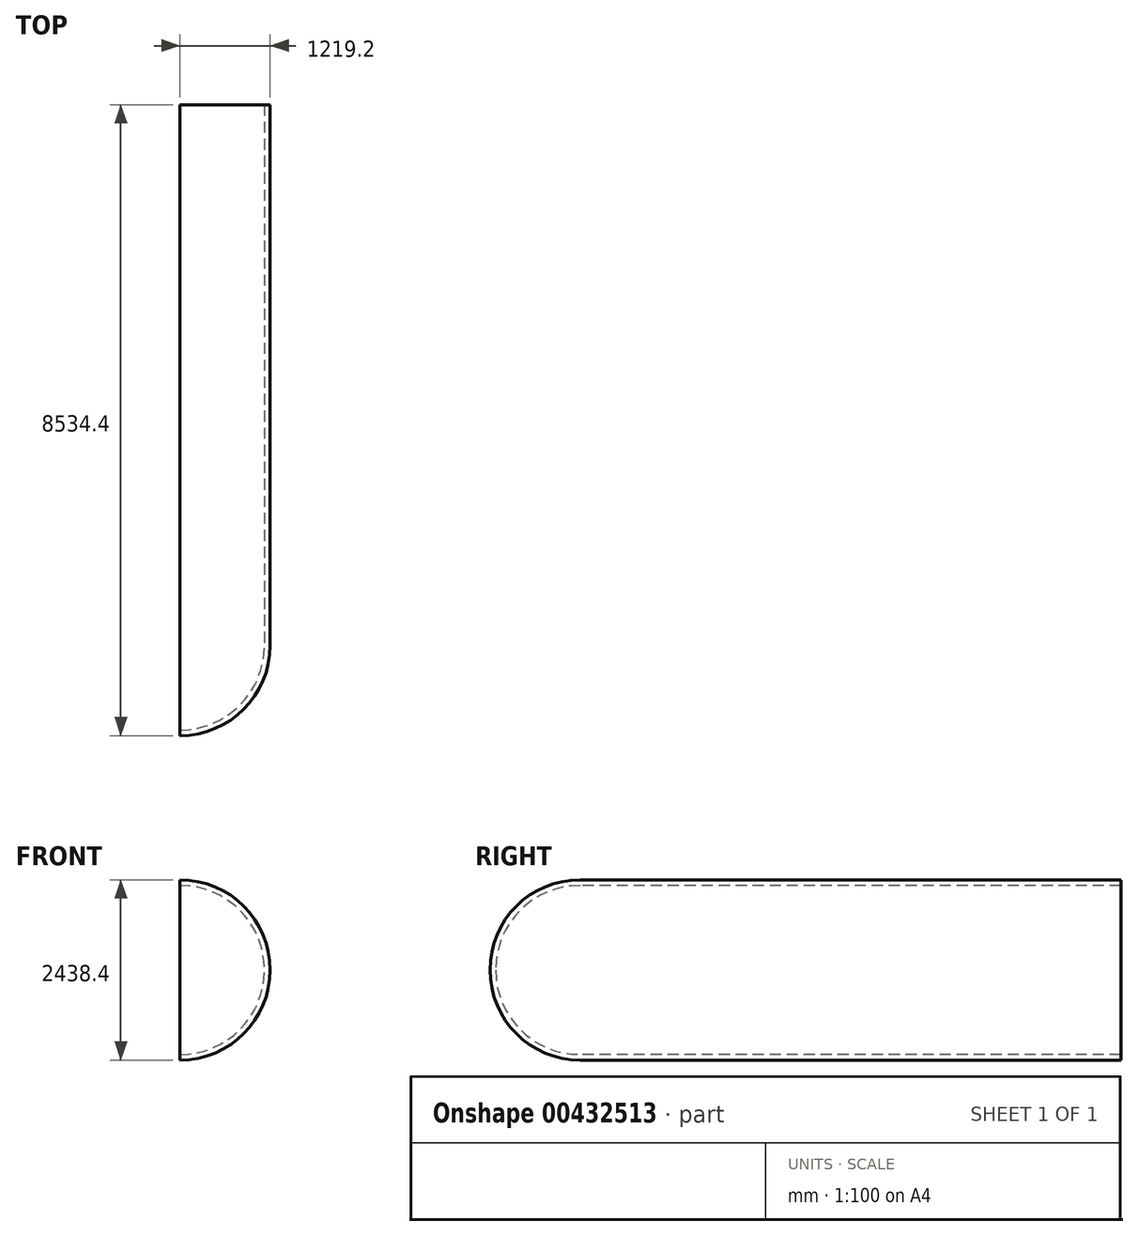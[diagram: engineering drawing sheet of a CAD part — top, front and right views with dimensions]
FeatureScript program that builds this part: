
annotation { "Feature Type Name" : "Feature", "Feature Type Description" : "" }
export const myFeature = defineFeature(function(context is Context, id is Id, definition is map)
    precondition{}
    {
        {
            var Q0;
            Q0=qCreatedBy(makeId("Right.planeOp"),FACE);
            var sketch = newSketch(context, id + "F0", { "sketchPlane" : qUnion([Q0])});
            skLineSegment(sketch, "E0.bottom", {"start": v(-3657.6, -1219.2) * mm, "end": v(3657.6, -1219.2) * mm});
            skLineSegment(sketch, "E0.top", {"start": v(-3657.6, 1219.2) * mm, "end": v(3657.6, 1219.2) * mm});
            skLineSegment(sketch, "E0.left", {"start": v(-3657.6, -1219.2) * mm, "end": v(-3657.6, 1219.2) * mm});
            skLineSegment(sketch, "E0.right", {"start": v(3657.6, -1219.2) * mm, "end": v(3657.6, 1219.2) * mm});
            skPoint(sketch, "E0.middle", {"position": v(0, 0) * mm});
            skLineSegment(sketch, "E1", {"start": v(-3657.6, 0) * mm, "end": v(3657.6, 0) * mm});
            skLineSegment(sketch, "E2", {"start": v(0, 1219.2) * mm, "end": v(0, -1219.2) * mm});
            skLineSegment(sketch, "E3", {"start": v(-1828.8, 1219.2) * mm, "end": v(-1828.8, -1219.2) * mm});
            skLineSegment(sketch, "E4", {"start": v(-914.4, 1219.2) * mm, "end": v(-914.4, -1219.2) * mm});
            skArc(sketch, "E5", {"start": v(-3657.6, -1219.2) * mm, "mid": v(-4876.8, 0) * mm, "end": v(-3657.6, 1219.2) * mm});
            skLineSegment(sketch, "E6.MirrorCS", {"start": v(914.4, 1219.2) * mm, "end": v(914.4, -1219.2) * mm});
            skLineSegment(sketch, "E7.MirrorCS", {"start": v(1828.8, 1219.2) * mm, "end": v(1828.8, -1219.2) * mm});
            skLineSegment(sketch, "E8.MirrorCS", {"start": v(2743.2, 1219.2) * mm, "end": v(2743.2, -1219.2) * mm});
            skLineSegment(sketch, "E9.MirrorCS", {"start": v(-2743.2, 1219.2) * mm, "end": v(-2743.2, -1219.2) * mm});
            skLineSegment(sketch, "E10.MirrorCS", {"start": v(-3657.6, 1219.2) * mm, "end": v(-3657.6, -1219.2) * mm});
            skLineSegment(sketch, "E11.MirrorCS", {"start": v(-4572, 1219.2) * mm, "end": v(-4572, -1219.2) * mm});
            skLineSegment(sketch, "E12", {"start": v(3657.6, 0) * mm, "end": v(4572, 0) * mm});
            skLineSegment(sketch, "E13", {"start": v(3657.6, 609.6) * mm, "end": v(-4713.46, 609.6) * mm});
            skLineSegment(sketch, "E14", {"start": v(3657.6, 914.4) * mm, "end": v(2743.2, 914.4) * mm});
            skPoint(sketch, "E14.startSnap0", {"position": v(3200.4, 914.4) * mm});
            skLineSegment(sketch, "E15", {"start": v(3657.6, 1066.8) * mm, "end": v(2743.2, 1066.8) * mm});
            skPoint(sketch, "E15.startSnap0", {"position": v(3200.4, 1066.8) * mm});
            skLineSegment(sketch, "E16", {"start": v(3657.6, 1143) * mm, "end": v(2743.2, 1143) * mm});
            skPoint(sketch, "E16.startSnap0", {"position": v(3200.4, 1143) * mm});
            skLineSegment(sketch, "E17", {"start": v(2743.2, 1066.8) * mm, "end": v(-3657.6, 1066.8) * mm});
            skArc(sketch, "E18", {"start": v(-3657.6, 1066.8) * mm, "mid": v(-4724.4, 0) * mm, "end": v(-3657.6, -1066.8) * mm});
            skLineSegment(sketch, "E19", {"start": v(-3657.6, -1066.8) * mm, "end": v(3657.6, -1066.8) * mm});
            skLineSegment(sketch, "E20", {"start": v(4572, -1066.8) * mm, "end": v(4572, -914.4) * mm});
            skLineSegment(sketch, "E21", {"start": v(4572, -914.4) * mm, "end": v(3657.6, -1066.8) * mm});
            skLineSegment(sketch, "E22", {"start": v(4572, -1066.8) * mm, "end": v(3657.6, -1219.2) * mm});
            skLineSegment(sketch, "E23", {"start": v(4572, 0) * mm, "end": v(4572, -914.4) * mm});
            skLineSegment(sketch, "E24", {"start": v(3657.6, 1066.8) * mm, "end": v(4572, 1066.8) * mm});
            skLineSegment(sketch, "E25", {"start": v(4572, 1066.8) * mm, "end": v(3657.6, 1219.2) * mm});
            skCircle(sketch, "E26", {"center": v(0, 0) * mm, "radius": 1066.8 * mm});
            skLineSegment(sketch, "E27", {"start": v(-4876.8, 0) * mm, "end": v(-4876.8, -1561.92) * mm});
            skLineSegment(sketch, "E28", {"start": v(2743.2, 1143) * mm, "end": v(-3657.6, 1143) * mm});
            skLineSegment(sketch, "E29", {"start": v(3657.6, -1143) * mm, "end": v(-3657.6, -1143) * mm});
            skArc(sketch, "E30", {"start": v(-3657.6, -1143) * mm, "mid": v(-4800.6, 0) * mm, "end": v(-3657.6, 1143) * mm});
            skLineSegment(sketch, "E31.MirrorCS", {"start": v(-3657.6, -762) * mm, "end": v(3657.6, -762) * mm});
            skLineSegment(sketch, "E32", {"start": v(-746.6, -762) * mm, "end": v(-746.6, 762) * mm});
            skLineSegment(sketch, "E33", {"start": v(0, -762) * mm, "end": v(0, 1066.8) * mm});
            skLineSegment(sketch, "E34", {"start": v(-1797.7, -3927.66) * mm, "end": v(-1774.84, -3927.66) * mm});
            skLineSegment(sketch, "E35", {"start": v(-1797.7, -3927.66) * mm, "end": v(-1797.7, -3930.2) * mm});
            skLineSegment(sketch, "E36", {"start": v(-1797.7, -3930.2) * mm, "end": v(-1772.8, -3930.2) * mm});
            skLineSegment(sketch, "E37", {"start": v(-1769.76, -3914.96) * mm, "end": v(-1769.76, -3912.42) * mm});
            skLineSegment(sketch, "E38", {"start": v(-1846.8, -3914.96) * mm, "end": v(-1846.8, -3912.42) * mm});
            skLineSegment(sketch, "E39", {"start": v(-1774.84, -3914.96) * mm, "end": v(-1774.84, -3927.66) * mm});
            skLineSegment(sketch, "E40", {"start": v(-1769.76, -3914.96) * mm, "end": v(-1772.8, -3930.2) * mm});
            skLineSegment(sketch, "E41", {"start": v(-1846.8, -3912.42) * mm, "end": v(-1769.76, -3912.42) * mm});
            skLineSegment(sketch, "E42", {"start": v(-1846.8, -3914.96) * mm, "end": v(-1774.84, -3914.96) * mm});
            skLineSegment(sketch, "E43.MirrorCS", {"start": v(-1769.76, -3914.96) * mm, "end": v(-1766.7, -3930.2) * mm});
            skLineSegment(sketch, "E44.MirrorCS", {"start": v(-1741.82, -3930.2) * mm, "end": v(-1766.7, -3930.2) * mm});
            skLineSegment(sketch, "E45.MirrorCS", {"start": v(-1741.82, -3927.66) * mm, "end": v(-1741.82, -3930.2) * mm});
            skLineSegment(sketch, "E46.MirrorCS", {"start": v(-1741.82, -3927.66) * mm, "end": v(-1764.68, -3927.66) * mm});
            skLineSegment(sketch, "E47.MirrorCS", {"start": v(-1764.68, -3914.96) * mm, "end": v(-1764.68, -3927.66) * mm});
            skLineSegment(sketch, "E48", {"start": v(-1772.55, -3930.2) * mm, "end": v(-1770.52, -3920.04) * mm});
            skLineSegment(sketch, "E49", {"start": v(-1772.55, -3930.2) * mm, "end": v(-1772.6, -3930.45) * mm});
            skLineSegment(sketch, "E50", {"start": v(-1772.6, -3930.45) * mm, "end": v(-1798, -3930.45) * mm});
            skLineSegment(sketch, "E51", {"start": v(-1798, -3930.45) * mm, "end": v(-1798, -3927.4) * mm});
            skLineSegment(sketch, "E52", {"start": v(-1798, -3927.4) * mm, "end": v(-1775.14, -3927.4) * mm});
            skLineSegment(sketch, "E53", {"start": v(-1775.14, -3927.4) * mm, "end": v(-1775.14, -3915.2) * mm});
            skLineSegment(sketch, "E54", {"start": v(-1775.14, -3915.2) * mm, "end": v(-1813.24, -3915.2) * mm});
            skLineSegment(sketch, "E55.MirrorCS", {"start": v(-1766.96, -3930.2) * mm, "end": v(-1769, -3920.04) * mm});
            skLineSegment(sketch, "E56.MirrorCS", {"start": v(-1766.91, -3930.45) * mm, "end": v(-1741.51, -3930.45) * mm});
            skLineSegment(sketch, "E57.MirrorCS", {"start": v(-1741.51, -3930.45) * mm, "end": v(-1741.51, -3927.4) * mm});
            skLineSegment(sketch, "E58.MirrorCS", {"start": v(-1741.51, -3927.4) * mm, "end": v(-1764.37, -3927.4) * mm});
            skLineSegment(sketch, "E59.MirrorCS", {"start": v(-1764.37, -3927.4) * mm, "end": v(-1764.37, -3915.2) * mm});
            skLineSegment(sketch, "E60.MirrorCS", {"start": v(-1764.37, -3915.2) * mm, "end": v(-1726.27, -3915.2) * mm});
            skLineSegment(sketch, "E61", {"start": v(-1769, -3920.04) * mm, "end": v(-1770.52, -3920.04) * mm});
            skLineSegment(sketch, "E62", {"start": v(-1766.91, -3930.45) * mm, "end": v(-1766.96, -3930.2) * mm});
            skLineSegment(sketch, "E63", {"start": v(-1813.24, -3935.52) * mm, "end": v(-1726.27, -3935.52) * mm});
            skLineSegment(sketch, "E64", {"start": v(-1813.24, -3935.52) * mm, "end": v(-1813.24, -3915.2) * mm});
            skLineSegment(sketch, "E65", {"start": v(-1726.27, -3915.2) * mm, "end": v(-1726.27, -3935.52) * mm});
            skCircle(sketch, "E66", {"center": v(-8660.7, 0) * mm, "radius": 1219.2 * mm});
            skLineSegment(sketch, "E67", {"start": v(-8660.7, 0) * mm, "end": v(-8660.7, 1219.2) * mm});
            skLineSegment(sketch, "E68", {"start": v(-8660.7, 0) * mm, "end": v(-8660.7, -1219.2) * mm});
            skLineSegment(sketch, "E69", {"start": v(-7441.5, 0) * mm, "end": v(-8660.7, 0) * mm});
            skLineSegment(sketch, "E70", {"start": v(-8051.1, -609.6) * mm, "end": v(-8660.7, -609.6) * mm});
            skPoint(sketch, "E70.startSnap0", {"position": v(-8051.1, 0) * mm});
            skPoint(sketch, "E70.startSnap1", {"position": v(-8660.7, -609.6) * mm});
            skLineSegment(sketch, "E71", {"start": v(-8355.9, -1180.49) * mm, "end": v(-8355.9, -609.6) * mm});
            skPoint(sketch, "E71.startSnap0", {"position": v(-8355.9, -609.6) * mm});
            skLineSegment(sketch, "E72", {"start": v(-8355.9, -895.04) * mm, "end": v(-7832.84, -895.04) * mm});
            skLineSegment(sketch, "E73", {"start": v(-8094.37, -1079.69) * mm, "end": v(-8094.37, -895.04) * mm});
            skPoint(sketch, "E73.startSnap0", {"position": v(-8094.37, -895.04) * mm});
            skLineSegment(sketch, "E74", {"start": v(-8355.9, -609.6) * mm, "end": v(-8355.9, 0) * mm});
            skLineSegment(sketch, "E75", {"start": v(-8355.9, 0) * mm, "end": v(-8051.1, 0) * mm});
            skLineSegment(sketch, "E76", {"start": v(-8051.1, -609.6) * mm, "end": v(-8051.1, 0) * mm});
            skLineSegment(sketch, "E77", {"start": v(-8051.1, -1055.86) * mm, "end": v(-8051.1, -609.6) * mm});
            skLineSegment(sketch, "E78", {"start": v(-8051.1, -609.6) * mm, "end": v(-7441.5, 0) * mm});
            skLineSegment(sketch, "E79", {"start": v(-7746.3, -304.8) * mm, "end": v(-7746.3, 0) * mm});
            skLineSegment(sketch, "E80", {"start": v(-7746.3, 0) * mm, "end": v(-7746.3, -806.42) * mm});
            skLineSegment(sketch, "E81", {"start": v(-8660.7, -304.8) * mm, "end": v(-7480.21, -304.8) * mm});
            skPoint(sketch, "E81.startSnap0", {"position": v(-8355.9, -304.8) * mm});
            skLineSegment(sketch, "E82", {"start": v(-8051.1, -609.6) * mm, "end": v(-7604.84, -609.6) * mm});
            skLineSegment(sketch, "E83.bottom", {"start": v(7784.68, -1157.92) * mm, "end": v(15099.88, -1157.92) * mm});
            skLineSegment(sketch, "E83.top", {"start": v(7784.68, 1280.48) * mm, "end": v(15099.88, 1280.48) * mm});
            skLineSegment(sketch, "E83.left", {"start": v(7784.68, -1157.92) * mm, "end": v(7784.68, 1280.48) * mm});
            skLineSegment(sketch, "E83.right", {"start": v(15099.88, -1157.92) * mm, "end": v(15099.88, 1280.48) * mm});
            skLineSegment(sketch, "E84", {"start": v(9613.48, 1280.48) * mm, "end": v(9613.48, -1157.92) * mm});
            skLineSegment(sketch, "E85", {"start": v(10527.88, 1280.48) * mm, "end": v(10527.88, -1157.92) * mm});
            skArc(sketch, "E86", {"start": v(7784.68, -1157.92) * mm, "mid": v(6565.48, 61.28) * mm, "end": v(7784.68, 1280.48) * mm});
            skLineSegment(sketch, "E87.MirrorCS", {"start": v(12356.68, 1280.48) * mm, "end": v(12356.68, -1157.92) * mm});
            skLineSegment(sketch, "E88.MirrorCS", {"start": v(13271.08, 1280.48) * mm, "end": v(13271.08, -1157.92) * mm});
            skLineSegment(sketch, "E89.MirrorCS", {"start": v(14185.48, 1280.48) * mm, "end": v(14185.48, -1157.92) * mm});
            skLineSegment(sketch, "E90.MirrorCS", {"start": v(8699.08, 1280.48) * mm, "end": v(8699.08, -1157.92) * mm});
            skLineSegment(sketch, "E91.MirrorCS", {"start": v(7784.68, 1280.48) * mm, "end": v(7784.68, -1157.92) * mm});
            skLineSegment(sketch, "E92.MirrorCS", {"start": v(6870.28, 610.76) * mm, "end": v(6870.28, -488.2) * mm});
            skLineSegment(sketch, "E93", {"start": v(15099.88, 61.28) * mm, "end": v(16014.28, 61.28) * mm});
            skLineSegment(sketch, "E94", {"start": v(15099.88, 1128.08) * mm, "end": v(14185.48, 1128.08) * mm});
            skLineSegment(sketch, "E95", {"start": v(15099.88, 1204.28) * mm, "end": v(14185.48, 1204.28) * mm});
            skLineSegment(sketch, "E96", {"start": v(14185.48, 1128.08) * mm, "end": v(7784.68, 1128.08) * mm});
            skArc(sketch, "E97", {"start": v(7784.68, 1128.08) * mm, "mid": v(6717.88, 61.28) * mm, "end": v(7784.68, -1005.52) * mm});
            skLineSegment(sketch, "E98", {"start": v(7784.68, -1005.52) * mm, "end": v(15099.88, -1005.52) * mm});
            skLineSegment(sketch, "E99", {"start": v(16014.28, -1005.52) * mm, "end": v(16014.28, -853.12) * mm});
            skLineSegment(sketch, "E100", {"start": v(16014.28, -853.12) * mm, "end": v(15099.88, -1005.52) * mm});
            skLineSegment(sketch, "E101", {"start": v(16014.28, -1005.52) * mm, "end": v(15099.88, -1157.92) * mm});
            skLineSegment(sketch, "E102", {"start": v(16014.28, 61.28) * mm, "end": v(16014.28, -853.12) * mm});
            skLineSegment(sketch, "E103", {"start": v(15099.88, 1128.08) * mm, "end": v(16014.28, 1128.08) * mm});
            skLineSegment(sketch, "E104", {"start": v(16014.28, 1128.08) * mm, "end": v(15099.88, 1280.48) * mm});
            skLineSegment(sketch, "E105", {"start": v(14185.48, 1204.28) * mm, "end": v(7784.68, 1204.28) * mm});
            skLineSegment(sketch, "E106", {"start": v(15099.88, -1081.72) * mm, "end": v(7784.68, -1081.72) * mm});
            skArc(sketch, "E107", {"start": v(7784.68, -1081.72) * mm, "mid": v(6641.68, 61.28) * mm, "end": v(7784.68, 1204.28) * mm});
            skLineSegment(sketch, "E108", {"start": v(11442.28, -1157.92) * mm, "end": v(11442.28, 1280.48) * mm});
            skLineSegment(sketch, "E109", {"start": v(-1726.27, -3935.52) * mm, "end": v(-1726.27, -3948.21) * mm});
            skLineSegment(sketch, "E110.MirrorCS", {"start": v(-1639.3, -3935.52) * mm, "end": v(-1726.27, -3935.52) * mm});
            skLineSegment(sketch, "E111.MirrorCS", {"start": v(-1711.03, -3930.45) * mm, "end": v(-1711.03, -3927.4) * mm});
            skLineSegment(sketch, "E112.MirrorCS", {"start": v(-1685.63, -3930.45) * mm, "end": v(-1711.03, -3930.45) * mm});
            skLineSegment(sketch, "E113.MirrorCS", {"start": v(-1710.73, -3930.2) * mm, "end": v(-1685.84, -3930.2) * mm});
            skLineSegment(sketch, "E114.MirrorCS", {"start": v(-1710.73, -3927.66) * mm, "end": v(-1710.73, -3930.2) * mm});
            skLineSegment(sketch, "E115.MirrorCS", {"start": v(-1710.73, -3927.66) * mm, "end": v(-1687.87, -3927.66) * mm});
            skLineSegment(sketch, "E116.MirrorCS", {"start": v(-1711.03, -3927.4) * mm, "end": v(-1688.17, -3927.4) * mm});
            skLineSegment(sketch, "E117.MirrorCS", {"start": v(-1688.17, -3927.4) * mm, "end": v(-1688.17, -3915.2) * mm});
            skLineSegment(sketch, "E118.MirrorCS", {"start": v(-1687.87, -3914.96) * mm, "end": v(-1687.87, -3927.66) * mm});
            skLineSegment(sketch, "E119.MirrorCS", {"start": v(-1682.79, -3914.96) * mm, "end": v(-1685.84, -3930.2) * mm});
            skLineSegment(sketch, "E120.MirrorCS", {"start": v(-1682.79, -3914.96) * mm, "end": v(-1682.79, -3912.42) * mm});
            skLineSegment(sketch, "E121.MirrorCS", {"start": v(-1688.17, -3915.2) * mm, "end": v(-1726.27, -3915.2) * mm});
            skLineSegment(sketch, "E122.MirrorCS", {"start": v(-1683.55, -3920.04) * mm, "end": v(-1682.03, -3920.04) * mm});
            skLineSegment(sketch, "E123.MirrorCS", {"start": v(-1685.58, -3930.2) * mm, "end": v(-1683.55, -3920.04) * mm});
            skLineSegment(sketch, "E124.MirrorCS", {"start": v(-1680, -3930.2) * mm, "end": v(-1682.03, -3920.04) * mm});
            skLineSegment(sketch, "E125.MirrorCS", {"start": v(-1679.94, -3930.45) * mm, "end": v(-1654.54, -3930.45) * mm});
            skLineSegment(sketch, "E126.MirrorCS", {"start": v(-1654.85, -3930.2) * mm, "end": v(-1679.74, -3930.2) * mm});
            skLineSegment(sketch, "E127.MirrorCS", {"start": v(-1654.54, -3927.4) * mm, "end": v(-1677.4, -3927.4) * mm});
            skLineSegment(sketch, "E128.MirrorCS", {"start": v(-1654.85, -3927.66) * mm, "end": v(-1677.7, -3927.66) * mm});
            skLineSegment(sketch, "E129.MirrorCS", {"start": v(-1677.4, -3927.4) * mm, "end": v(-1677.4, -3915.2) * mm});
            skLineSegment(sketch, "E130.MirrorCS", {"start": v(-1677.7, -3914.96) * mm, "end": v(-1677.7, -3927.66) * mm});
            skLineSegment(sketch, "E131.MirrorCS", {"start": v(-1677.4, -3915.2) * mm, "end": v(-1639.3, -3915.2) * mm});
            skLineSegment(sketch, "E132.MirrorCS", {"start": v(-1605.74, -3914.96) * mm, "end": v(-1677.7, -3914.96) * mm});
            skLineSegment(sketch, "E133.MirrorCS", {"start": v(-1605.74, -3912.42) * mm, "end": v(-1682.79, -3912.42) * mm});
            skLineSegment(sketch, "E134.MirrorCS", {"start": v(-1682.79, -3914.96) * mm, "end": v(-1679.74, -3930.2) * mm});
            skLineSegment(sketch, "E135.MirrorCS", {"start": v(-1639.3, -3935.52) * mm, "end": v(-1639.3, -3915.2) * mm});
            skLineSegment(sketch, "E136.MirrorCS", {"start": v(-1605.74, -3914.96) * mm, "end": v(-1605.74, -3912.42) * mm});
            skLineSegment(sketch, "E137", {"start": v(-1769.76, -3912.42) * mm, "end": v(-1682.79, -3912.42) * mm});
            skLineSegment(sketch, "E138", {"start": v(-1764.68, -3914.96) * mm, "end": v(-1687.87, -3914.96) * mm});
            skLineSegment(sketch, "E139", {"start": v(-1654.85, -3927.66) * mm, "end": v(-1654.85, -3930.2) * mm});
            skLineSegment(sketch, "E140", {"start": v(-1654.54, -3927.4) * mm, "end": v(-1654.54, -3930.45) * mm});
            skLineSegment(sketch, "E141", {"start": v(-1685.63, -3930.45) * mm, "end": v(-1685.58, -3930.2) * mm});
            skLineSegment(sketch, "E142", {"start": v(-1679.94, -3930.45) * mm, "end": v(-1680, -3930.2) * mm});
            skLineSegment(sketch, "E143", {"start": v(-1592.05, -3912.42) * mm, "end": v(-1592.05, -3937.82) * mm, "construction": true});
            skLineSegment(sketch, "E144", {"start": v(-1592.05, -3937.82) * mm, "end": v(-1592.05, -3963.22) * mm, "construction": true});
            skLineSegment(sketch, "E145", {"start": v(-1592.05, -3963.22) * mm, "end": v(-1592.05, -3988.62) * mm, "construction": true});
            skLineSegment(sketch, "E146", {"start": v(-1639.3, -3921.3) * mm, "end": v(-1635.47, -3921.3) * mm});
            skPoint(sketch, "E146.startSnap0", {"position": v(-1677.4, -3921.3) * mm});
            skPoint(sketch, "E146.endSnap0", {"position": v(-1677.4, -3921.3) * mm});
            skLineSegment(sketch, "E147", {"start": v(-1635.47, -3921.3) * mm, "end": v(-1635.47, -3922.57) * mm});
            skLineSegment(sketch, "E148.MirrorCS", {"start": v(-1635.47, -3921.3) * mm, "end": v(-1635.47, -3920.03) * mm});
            skLineSegment(sketch, "E149", {"start": v(-1635.47, -3920.03) * mm, "end": v(-1677.4, -3920.03) * mm});
            skLineSegment(sketch, "E150", {"start": v(-1677.4, -3920.03) * mm, "end": v(-1677.4, -3922.57) * mm});
            skLineSegment(sketch, "E151", {"start": v(-1677.4, -3922.57) * mm, "end": v(-1635.47, -3922.57) * mm});
            skLineSegment(sketch, "E152", {"start": v(-1685.58, -3930.2) * mm, "end": v(-1686.65, -3935.52) * mm});
            skLineSegment(sketch, "E153", {"start": v(-1686.65, -3935.52) * mm, "end": v(-1683.55, -3930.2) * mm});
            skLineSegment(sketch, "E154", {"start": v(-1683.55, -3930.2) * mm, "end": v(-1682.03, -3930.2) * mm});
            skLineSegment(sketch, "E155.MirrorCS", {"start": v(-1678.93, -3935.52) * mm, "end": v(-1682.03, -3930.2) * mm});
            skLineSegment(sketch, "E156.MirrorCS", {"start": v(-1680, -3930.2) * mm, "end": v(-1678.93, -3935.52) * mm});
            skLineSegment(sketch, "E157", {"start": v(6717.88, 61.28) * mm, "end": v(6565.48, 61.28) * mm});
            skSolve(sketch);
        }
        {
            var Q0;
            {var subQ1=sQuery(id+"F0.wireOp",EDGE,"E86");var subQ3=sQuery(id+"F0.wireOp",EDGE,"E157");var subQ4=makeQuery(id+"F0.imprint","INTERSECT",VERTEX,{"derivedFrom":[subQ1,subQ3]});Q0=makeQuery(id+"F0.imprint","IMPRINT",FACE,{"disambiguationData":[TD([[makeQuery(id+"F0.imprint","IMPRINT",EDGE,{"disambiguationData":[TD([[subQ4,1.0]])],"derivedFrom":subQ3}),-1.0]])]});}
            var Q1;
            {var subQ1=sQuery(id+"F0.wireOp",EDGE,"E83.top");var subQ3=sQuery(id+"F0.wireOp",EDGE,"E90.MirrorCS");var subQ4=makeQuery(id+"F0.imprint","INTERSECT",VERTEX,{"derivedFrom":[subQ1,subQ3]});Q1=makeQuery(id+"F0.imprint","IMPRINT",FACE,{"disambiguationData":[TD([[makeQuery(id+"F0.imprint","IMPRINT",EDGE,{"disambiguationData":[TD([[subQ4,-1.0]])],"derivedFrom":subQ3}),-1.0]])]});}
            var Q2;
            {var subQ0=sQuery(id+"F0.wireOp",EDGE,"E84");var subQ1=sQuery(id+"F0.wireOp",EDGE,"E83.top");var subQ2=makeQuery(id+"F0.imprint","INTERSECT",VERTEX,{"derivedFrom":[subQ1,subQ0]});Q2=makeQuery(id+"F0.imprint","IMPRINT",FACE,{"disambiguationData":[TD([[makeQuery(id+"F0.imprint","IMPRINT",EDGE,{"disambiguationData":[TD([[subQ2,1.0]])],"derivedFrom":subQ1}),-1.0]])]});}
            var Q3;
            {var subQ0=sQuery(id+"F0.wireOp",EDGE,"E84");var subQ1=sQuery(id+"F0.wireOp",EDGE,"E83.top");var subQ2=makeQuery(id+"F0.imprint","INTERSECT",VERTEX,{"derivedFrom":[subQ1,subQ0]});Q3=makeQuery(id+"F0.imprint","IMPRINT",FACE,{"disambiguationData":[TD([[makeQuery(id+"F0.imprint","IMPRINT",EDGE,{"disambiguationData":[TD([[subQ2,-1.0]])],"derivedFrom":subQ1}),-1.0]])]});}
            var Q4;
            {var subQ0=sQuery(id+"F0.wireOp",EDGE,"E85");var subQ1=sQuery(id+"F0.wireOp",EDGE,"E83.top");var subQ2=makeQuery(id+"F0.imprint","INTERSECT",VERTEX,{"derivedFrom":[subQ1,subQ0]});Q4=makeQuery(id+"F0.imprint","IMPRINT",FACE,{"disambiguationData":[TD([[makeQuery(id+"F0.imprint","IMPRINT",EDGE,{"disambiguationData":[TD([[subQ2,-1.0]])],"derivedFrom":subQ1}),-1.0]])]});}
            var Q5;
            {var subQ0=sQuery(id+"F0.wireOp",EDGE,"E87.MirrorCS");var subQ1=sQuery(id+"F0.wireOp",EDGE,"E83.top");var subQ2=makeQuery(id+"F0.imprint","INTERSECT",VERTEX,{"derivedFrom":[subQ1,subQ0]});Q5=makeQuery(id+"F0.imprint","IMPRINT",FACE,{"disambiguationData":[TD([[makeQuery(id+"F0.imprint","IMPRINT",EDGE,{"disambiguationData":[TD([[subQ2,1.0]])],"derivedFrom":subQ1}),-1.0]])]});}
            var Q6;
            {var subQ0=sQuery(id+"F0.wireOp",EDGE,"E87.MirrorCS");var subQ1=sQuery(id+"F0.wireOp",EDGE,"E83.top");var subQ2=makeQuery(id+"F0.imprint","INTERSECT",VERTEX,{"derivedFrom":[subQ1,subQ0]});Q6=makeQuery(id+"F0.imprint","IMPRINT",FACE,{"disambiguationData":[TD([[makeQuery(id+"F0.imprint","IMPRINT",EDGE,{"disambiguationData":[TD([[subQ2,-1.0]])],"derivedFrom":subQ1}),-1.0]])]});}
            var Q7;
            {var subQ0=sQuery(id+"F0.wireOp",EDGE,"E88.MirrorCS");var subQ1=sQuery(id+"F0.wireOp",EDGE,"E83.top");var subQ2=makeQuery(id+"F0.imprint","INTERSECT",VERTEX,{"derivedFrom":[subQ1,subQ0]});Q7=makeQuery(id+"F0.imprint","IMPRINT",FACE,{"disambiguationData":[TD([[makeQuery(id+"F0.imprint","IMPRINT",EDGE,{"disambiguationData":[TD([[subQ2,-1.0]])],"derivedFrom":subQ1}),-1.0]])]});}
            var Q8;
            {var subQ5=sQuery(id+"F0.wireOp",EDGE,"E95");Q8=makeQuery(id+"F0.imprint","IMPRINT",FACE,{"disambiguationData":[TD([[makeQuery(id+"F0.imprint","IMPRINT",EDGE,{"derivedFrom":subQ5}),-1.0]])]});}
            var Q9;
            Q9=sQuery(id+"F0.wireOp",EDGE,"E93");
            revolve(context, id + "F1", {"entities" : qUnion([Q0, Q1, Q2, Q3, Q4, Q5, Q6, Q7, Q8]), "axis" : qUnion([Q9]), "revolveType" : RevolveType.ONE_DIRECTION, "angle" : 180 * degree});
        }
    });
